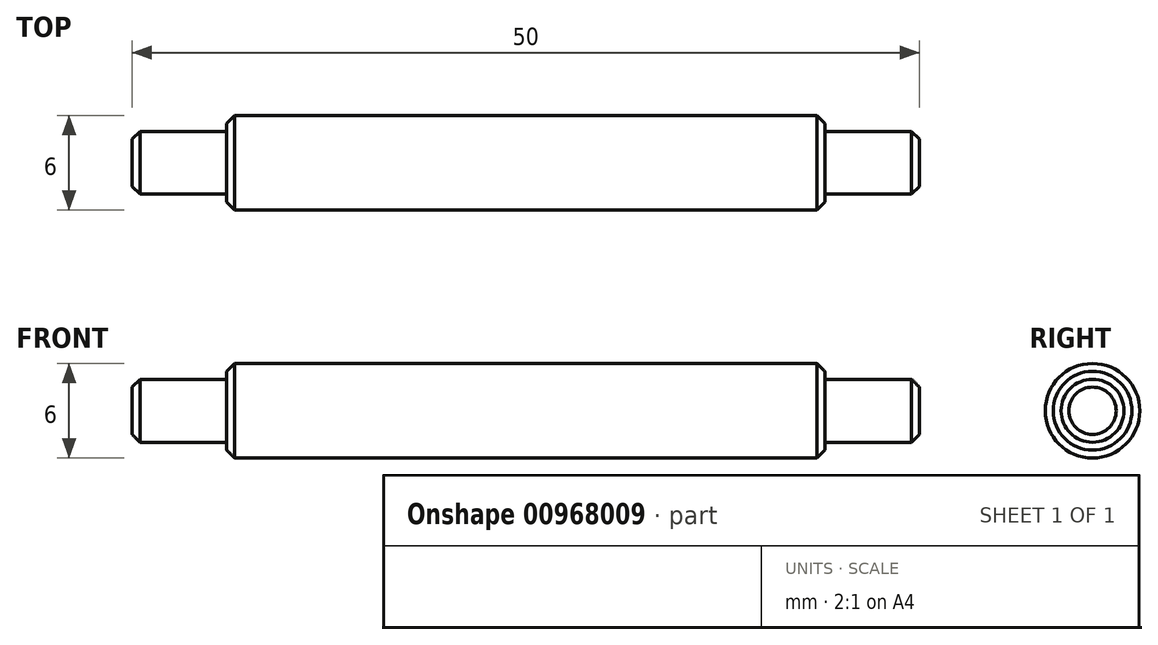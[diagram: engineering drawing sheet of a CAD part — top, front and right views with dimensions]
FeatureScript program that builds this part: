
annotation { "Feature Type Name" : "Feature", "Feature Type Description" : "" }
export const myFeature = defineFeature(function(context is Context, id is Id, definition is map)
    precondition{}
    {
        {
            var Q0;
            Q0=qCreatedBy(makeId("Front.planeOp"),FACE);
            var sketch = newSketch(context, id + "F0", { "sketchPlane" : qUnion([Q0])});
            skLineSegment(sketch, "E0", {"start": v(0, 0) * mm, "end": v(50, 0) * mm});
            skLineSegment(sketch, "E1", {"start": v(50, 0) * mm, "end": v(50, 2) * mm});
            skLineSegment(sketch, "E2", {"start": v(50, 2) * mm, "end": v(44, 2) * mm});
            skLineSegment(sketch, "E3", {"start": v(44, 2) * mm, "end": v(44, 3) * mm});
            skLineSegment(sketch, "E4", {"start": v(44, 3) * mm, "end": v(6, 3) * mm});
            skLineSegment(sketch, "E5", {"start": v(6, 3) * mm, "end": v(6, 2) * mm});
            skLineSegment(sketch, "E6", {"start": v(6, 2) * mm, "end": v(0, 2) * mm});
            skLineSegment(sketch, "E7", {"start": v(0, 2) * mm, "end": v(0, 0) * mm});
            skSolve(sketch);
        }
        {
            var Q0;
            Q0=makeQuery(id+"F0.imprint","IMPRINT",FACE,{"disambiguationData":[TD([[makeQuery(id+"F0.imprint","IMPRINT",EDGE,{"derivedFrom":sQuery(id+"F0.wireOp",EDGE,"E0")}),1.0]])]});
            var Q1;
            Q1=sQuery(id+"F0.wireOp",EDGE,"E0");
            revolve(context, id + "F1", {"surfaceOperationType" : NewSurfaceOperationType.NEW, "entities" : qUnion([Q0]), "axis" : qUnion([Q1]), "revolveType" : RevolveType.FULL});
        }
        {
            var Q0;
            Q0=makeQuery(id+"F1.opRevolve","SWEPT_EDGE",EDGE,{"disambiguationData":[OSD([sQuery(id+"F0.wireOp",EDGE,"E6"),sQuery(id+"F0.wireOp",EDGE,"E7")])]});
            var Q1;
            Q1=makeQuery(id+"F1.opRevolve","SWEPT_EDGE",EDGE,{"disambiguationData":[OSD([sQuery(id+"F0.wireOp",EDGE,"E1"),sQuery(id+"F0.wireOp",EDGE,"E2")])]});
            var Q2;
            Q2=makeQuery(id+"F1.opRevolve","SWEPT_EDGE",EDGE,{"disambiguationData":[OSD([sQuery(id+"F0.wireOp",EDGE,"E3"),sQuery(id+"F0.wireOp",EDGE,"E4")])]});
            var Q3;
            Q3=makeQuery(id+"F1.opRevolve","SWEPT_EDGE",EDGE,{"disambiguationData":[OSD([sQuery(id+"F0.wireOp",EDGE,"E4"),sQuery(id+"F0.wireOp",EDGE,"E5")])]});
            chamfer(context, id + "F2", {"entities" : qUnion([Q0, Q1, Q2, Q3]), "width" : .5 * mm, "tangentPropagation" : true});
        }
    });
